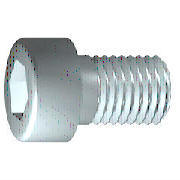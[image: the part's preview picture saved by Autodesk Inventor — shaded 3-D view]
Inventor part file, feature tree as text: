
AUTODESK INVENTOR PART (.ipt)
format: ipt  version: 2014 (Build 180170000, 170)  size: 181,760 bytes
history: native  units: mm (DEFAULTED — no unit token found)
features: sketch x2, extrude x1, plane x1, fillet x1
ambient origin geometry x7: Origin, YZ Plane, XY Plane, X Axis, Y Axis, Z Axis, Center Point
bodies: Solid1 (feature_tree), Body (feature_tree)
feature tree (5):
  extrude  "Slot"  Depth=1.5876mm
  plane  "Work Plane1"
  fillet  "Fillet2"  Radius=3.175mm
  sketch  "Sketch1"  dims[d1=19.05mm d2=1.5876mm d3=3.175mm]
  sketch  "Sketch2"  dims[d4=1.4478mm d5=60.0deg d6=3.175mm d7=3.175mm d8=2.756963mm d9=5.207mm d10=90.0deg d11=10.0mm d12=0.0mm d13=19.05mm d14=0.0mm d15=0.37846mm d16=0.37846mm d17=0.3048mm d19=0.0mm d26=38.1mm d27=45.0deg d28=0.0mm d29=0.0mm d30=0.127mm]
